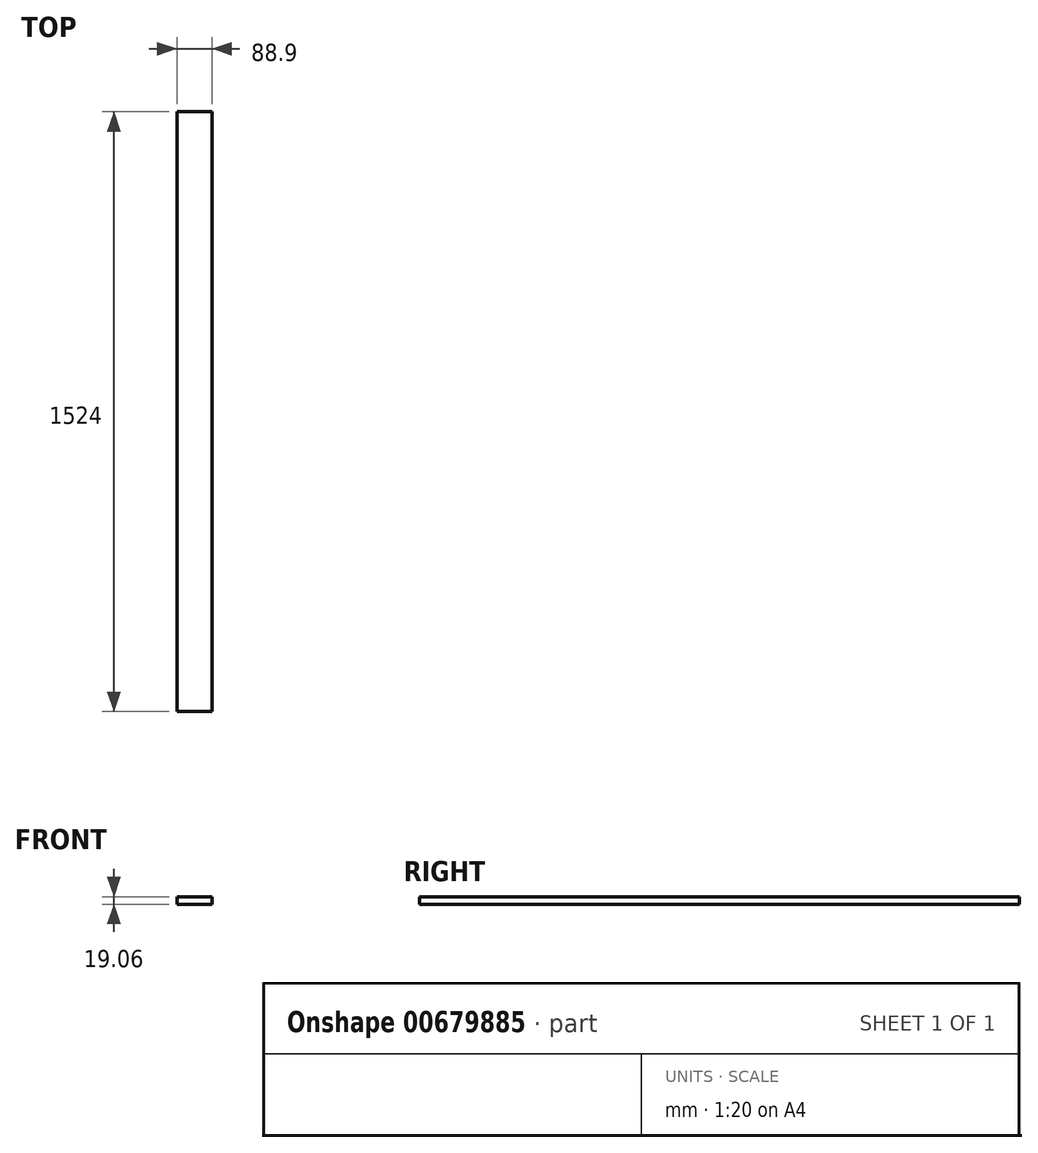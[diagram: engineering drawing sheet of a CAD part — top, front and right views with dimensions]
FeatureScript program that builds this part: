
annotation { "Feature Type Name" : "Feature", "Feature Type Description" : "" }
export const myFeature = defineFeature(function(context is Context, id is Id, definition is map)
    precondition{}
    {
        {
            var Q0;
            Q0=qCreatedBy(makeId("Front.planeOp"),FACE);
            var sketch = newSketch(context, id + "F0", { "sketchPlane" : qUnion([Q0])});
            skLineSegment(sketch, "E0.bottom", {"start": v(44.45, 9.53) * mm, "end": v(-44.45, 9.53) * mm});
            skLineSegment(sketch, "E0.top", {"start": v(44.45, -9.53) * mm, "end": v(-44.45, -9.53) * mm});
            skLineSegment(sketch, "E0.left", {"start": v(44.45, 9.53) * mm, "end": v(44.45, -9.53) * mm});
            skLineSegment(sketch, "E0.right", {"start": v(-44.45, 9.53) * mm, "end": v(-44.45, -9.52) * mm});
            skPoint(sketch, "E0.middle", {"position": v(0, 0) * mm});
            skSolve(sketch);
        }
        {
            var Q0;
            Q0=makeQuery(id+"F0.imprint","IMPRINT",FACE,{"disambiguationData":[TD([[makeQuery(id+"F0.imprint","IMPRINT",EDGE,{"derivedFrom":sQuery(id+"F0.wireOp",EDGE,"E0.bottom")}),1.0]])]});
            extrude(context, id + "F1", {"entities" : qUnion([Q0]), "endBound" : BoundingType.SYMMETRIC, "depth" : 1524 * mm, "offsetDistance" : 25.4 * mm});
        }
    });
